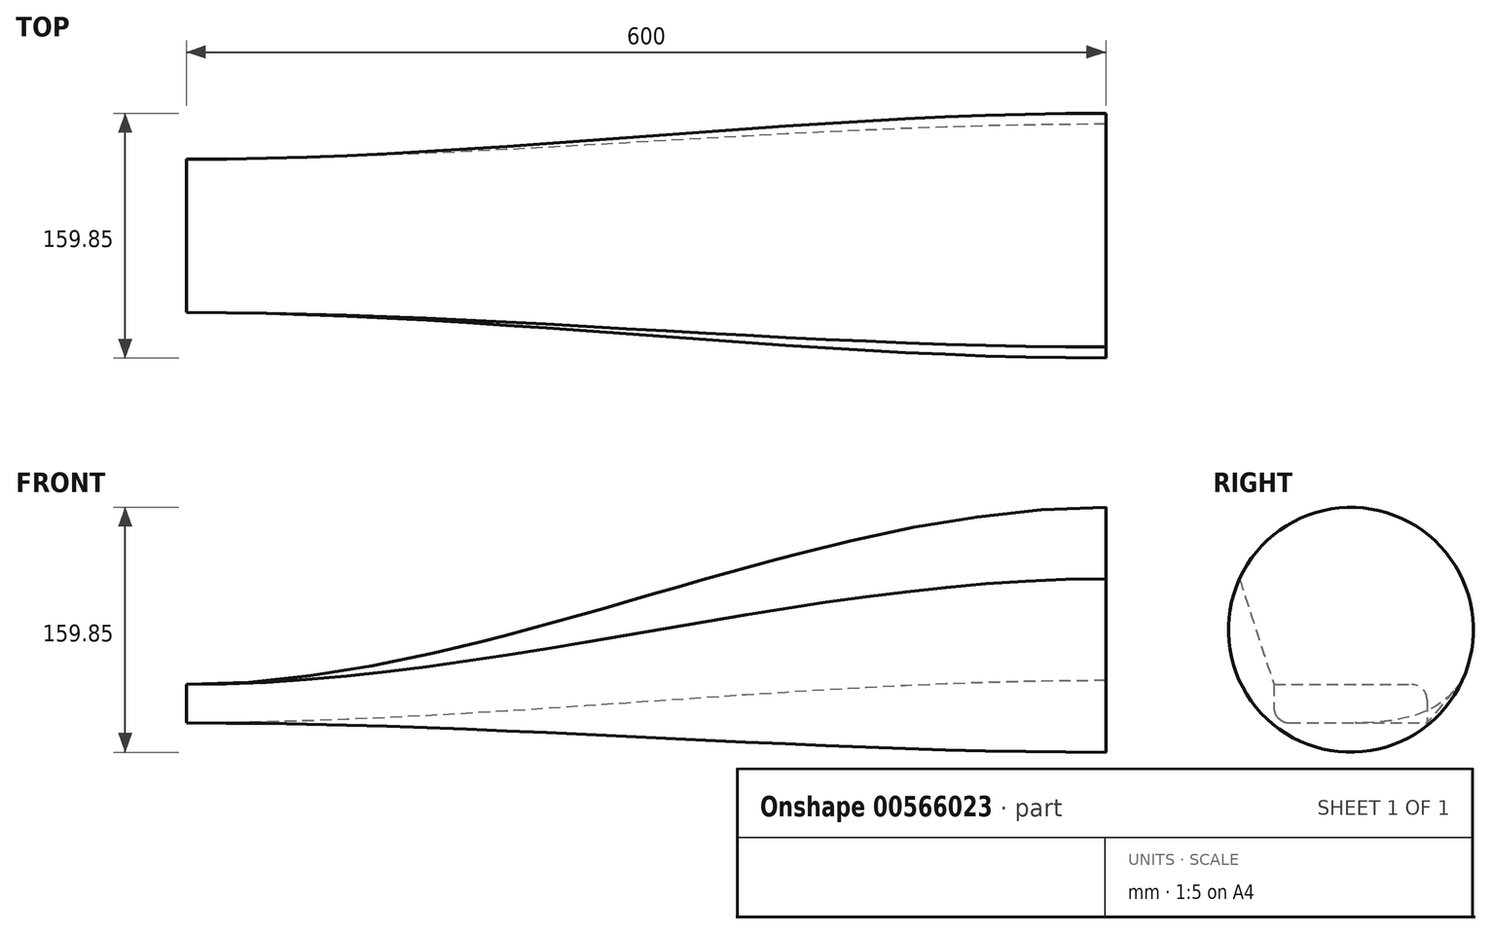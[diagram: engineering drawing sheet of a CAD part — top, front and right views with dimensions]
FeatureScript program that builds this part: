
annotation { "Feature Type Name" : "Feature", "Feature Type Description" : "" }
export const myFeature = defineFeature(function(context is Context, id is Id, definition is map)
    precondition{}
    {
        {
            var Q0;
            Q0=qCreatedBy(makeId("Right.planeOp"),FACE);
            var sketch = newSketch(context, id + "F0", { "sketchPlane" : qUnion([Q0])});
            skLineSegment(sketch, "E0.bottom", {"start": v(-106.05, 68.22) * mm, "end": v(-16.05, 68.22) * mm});
            skLineSegment(sketch, "E0.top", {"start": v(-96.05, 43.22) * mm, "end": v(-6.05, 43.22) * mm});
            skLineSegment(sketch, "E0.left", {"start": v(-106.05, 68.22) * mm, "end": v(-106.05, 53.22) * mm});
            skLineSegment(sketch, "E0.right", {"start": v(-6.05, 58.22) * mm, "end": v(-6.05, 43.22) * mm});
            skLineSegment(sketch, "E1.bottom", {"start": v(79.37, -110.55) * mm, "end": v(97.4, -110.55) * mm});
            skLineSegment(sketch, "E1.top", {"start": v(79.37, -82.37) * mm, "end": v(97.4, -82.37) * mm});
            skLineSegment(sketch, "E1.left", {"start": v(79.37, -110.55) * mm, "end": v(79.37, -82.37) * mm});
            skLineSegment(sketch, "E1.right", {"start": v(97.4, -110.55) * mm, "end": v(97.4, -82.37) * mm});
            skPoint(sketch, "E2.visualSharp", {"position": v(-106.05, 43.22) * mm});
            skArc(sketch, "E2.filletArc", {"start": v(-106.05, 53.22) * mm, "mid": v(-103.12, 46.15) * mm, "end": v(-96.05, 43.22) * mm});
            skPoint(sketch, "E3.visualSharp", {"position": v(-6.05, 68.22) * mm});
            skArc(sketch, "E3.filletArc", {"start": v(-6.05, 58.22) * mm, "mid": v(-8.98, 65.3) * mm, "end": v(-16.05, 68.22) * mm});
            skSolve(sketch);
        }
        {
            var Q0;
            Q0=qCreatedBy(makeId("Right.planeOp"),FACE);
            cPlane(context, id + "F1", {"entities" : qUnion([Q0]), "cplaneType" : CPlaneType.OFFSET, "offset" : 600 * mm, "width" : 152.4 * mm, "height" : 152.4 * mm});
        }
        {
            var Q0;
            Q0=qCreatedBy(id+"F1.planeOp",FACE);
            var sketch = newSketch(context, id + "F2", { "sketchPlane" : qUnion([Q0])});
            skCircle(sketch, "E4", {"center": v(-55.84, 104) * mm, "radius": 79.92 * mm});
            skSolve(sketch);
        }
        {
            var Q0;
            Q0 = qSketchRegion(id + "F2", true);
            var Q1;
            Q1=makeQuery(id+"F0.imprint","IMPRINT",FACE,{"disambiguationData":[TD([[makeQuery(id+"F0.imprint","IMPRINT",EDGE,{"derivedFrom":sQuery(id+"F0.wireOp",EDGE,"E0.bottom")}),-1.0]])]});
            loft(context, id + "F3", {"startCondition" : LoftEndDerivativeType.NORMAL_TO_PROFILE, "startMagnitude" : 1, "endCondition" : LoftEndDerivativeType.NORMAL_TO_PROFILE, "endMagnitude" : 1, "sheetProfilesArray" : [{ "sheetProfileEntities" : qUnion([Q0]) }, { "sheetProfileEntities" : qUnion([Q1]) }]});
        }
    });
